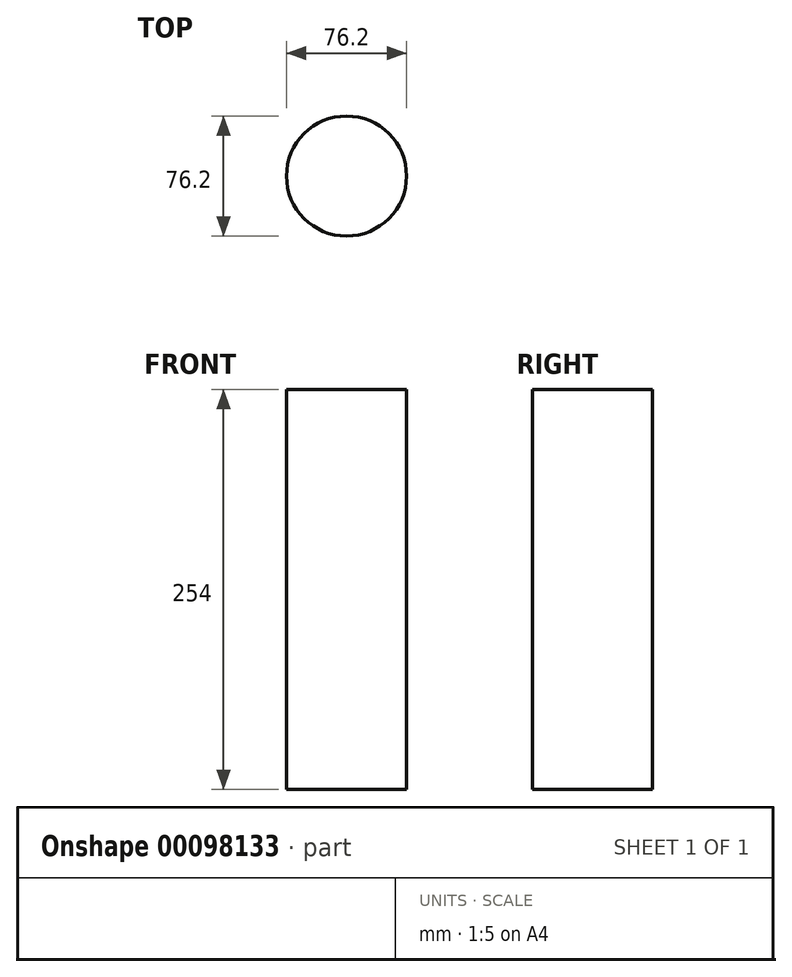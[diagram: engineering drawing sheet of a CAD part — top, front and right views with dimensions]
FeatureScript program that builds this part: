
annotation { "Feature Type Name" : "Feature", "Feature Type Description" : "" }
export const myFeature = defineFeature(function(context is Context, id is Id, definition is map)
    precondition{}
    {
        {
            var Q0;
            Q0=qCreatedBy(makeId("Top.planeOp"),FACE);
            var sketch = newSketch(context, id + "F0", { "sketchPlane" : qUnion([Q0])});
            skCircle(sketch, "E0", {"center": v(0, 0) * mm, "radius": 38.1 * mm});
            skSolve(sketch);
        }
        {
            var Q0;
            Q0 = qSketchRegion(id + "F0", true);
            var Q1;
            Q1=makeQuery(id+"F0.imprint","IMPRINT",FACE,{"disambiguationData":[TD([[makeQuery(id+"F0.imprint","IMPRINT",EDGE,{"derivedFrom":sQuery(id+"F0.wireOp",EDGE,"E0")}),1.0]])]});
            extrude(context, id + "F1", {"entities" : qUnion([Q0, Q1]), "depth" : 254 * mm});
        }
        {
            var Q0;
            Q0=qCreatedBy(makeId("Front.planeOp"),FACE);
            var sketch = newSketch(context, id + "F2", { "sketchPlane" : qUnion([Q0])});
            skLineSegment(sketch, "E1", {"start": v(0, 287.76) * mm, "end": v(0, 307.68) * mm});
            skLineSegment(sketch, "E2", {"start": v(0, 307.68) * mm, "end": v(6.02, 307.68) * mm});
            skLineSegment(sketch, "E3", {"start": v(6.02, 307.68) * mm, "end": v(6.02, 295.14) * mm});
            skLineSegment(sketch, "E4", {"start": v(6.02, 295.14) * mm, "end": v(36.28, 295.14) * mm});
            skLineSegment(sketch, "E5", {"start": v(36.28, 295.14) * mm, "end": v(36.28, 286.28) * mm});
            skLineSegment(sketch, "E6", {"start": v(36.28, 286.28) * mm, "end": v(0, 286.28) * mm});
            skLineSegment(sketch, "E7", {"start": v(-38.27, 281.85) * mm, "end": v(36.28, 281.85) * mm});
            skSolve(sketch);
        }
    });
